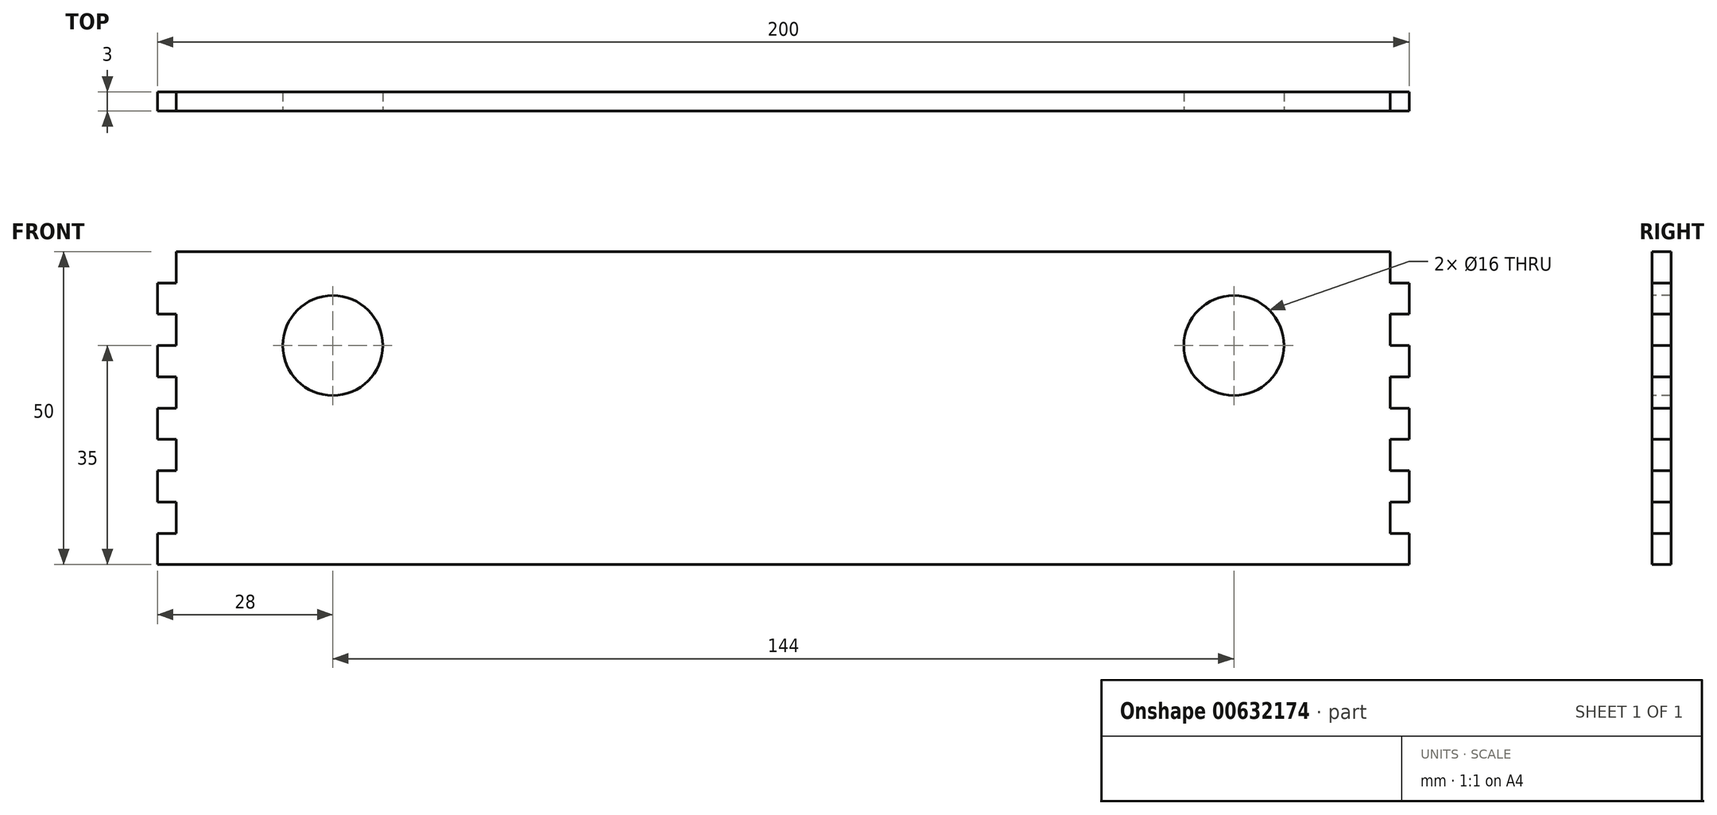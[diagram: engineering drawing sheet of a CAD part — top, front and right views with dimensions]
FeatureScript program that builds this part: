
annotation { "Feature Type Name" : "Feature", "Feature Type Description" : "" }
export const myFeature = defineFeature(function(context is Context, id is Id, definition is map)
    precondition{}
    {
        {
            var Q0;
            Q0=qCreatedBy(makeId("Front.planeOp"),FACE);
            var sketch = newSketch(context, id + "F0", { "sketchPlane" : qUnion([Q0])});
            skLineSegment(sketch, "E0.bottom", {"start": v(97, 25) * mm, "end": v(-97, 25) * mm});
            skLineSegment(sketch, "E0.top", {"start": v(97, -25) * mm, "end": v(-97, -25) * mm});
            skLineSegment(sketch, "E0.left", {"start": v(97, 25) * mm, "end": v(97, -25) * mm});
            skLineSegment(sketch, "E0.right", {"start": v(-97, 25) * mm, "end": v(-97, -25) * mm});
            skPoint(sketch, "E0.middle", {"position": v(0, 0) * mm});
            skSolve(sketch);
        }
        {
            var Q0;
            Q0=makeQuery(id+"F0.imprint","IMPRINT",FACE,{"disambiguationData":[TD([[makeQuery(id+"F0.imprint","IMPRINT",EDGE,{"derivedFrom":sQuery(id+"F0.wireOp",EDGE,"E0.bottom")}),1.0]])]});
            extrude(context, id + "F1", {"entities" : qUnion([Q0]), "depth" : 3 * mm, "offsetDistance" : 25 * mm});
        }
        {
            var Q0;
            Q0=makeQuery(id+"F1.opExtrude","CAP_FACE",FACE,{"disambiguationData":[OSD([sQuery(id+"F0.wireOp",EDGE,"E0.bottom"),sQuery(id+"F0.wireOp",EDGE,"E0.top"),sQuery(id+"F0.wireOp",EDGE,"E0.left"),sQuery(id+"F0.wireOp",EDGE,"E0.right")])],"isStart":false});
            var sketch = newSketch(context, id + "F2", { "sketchPlane" : qUnion([Q0])});
            skLineSegment(sketch, "E1.bottom", {"start": v(-97, 20) * mm, "end": v(-100, 20) * mm});
            skLineSegment(sketch, "E1.top", {"start": v(-97, 15) * mm, "end": v(-100, 15) * mm});
            skLineSegment(sketch, "E1.left", {"start": v(-97, 20) * mm, "end": v(-97, 15) * mm});
            skLineSegment(sketch, "E1.right", {"start": v(-100, 20) * mm, "end": v(-100, 15) * mm});
            skLineSegment(sketch, "E2.0.1.0", {"start": v(-97, 10) * mm, "end": v(-100, 10) * mm});
            skLineSegment(sketch, "E2.0.1.1", {"start": v(-97, 5) * mm, "end": v(-100, 5) * mm});
            skLineSegment(sketch, "E2.0.1.2", {"start": v(-97, 10) * mm, "end": v(-97, 5) * mm});
            skLineSegment(sketch, "E2.0.1.3", {"start": v(-100, 10) * mm, "end": v(-100, 5) * mm});
            skLineSegment(sketch, "E2.0.2.0", {"start": v(-97, 0) * mm, "end": v(-100, 0) * mm});
            skLineSegment(sketch, "E2.0.2.1", {"start": v(-97, -5) * mm, "end": v(-100, -5) * mm});
            skLineSegment(sketch, "E2.0.2.2", {"start": v(-97, 0) * mm, "end": v(-97, -5) * mm});
            skLineSegment(sketch, "E2.0.2.3", {"start": v(-100, 0) * mm, "end": v(-100, -5) * mm});
            skLineSegment(sketch, "E2.0.3.0", {"start": v(-97, -10) * mm, "end": v(-100, -10) * mm});
            skLineSegment(sketch, "E2.0.3.1", {"start": v(-97, -15) * mm, "end": v(-100, -15) * mm});
            skLineSegment(sketch, "E2.0.3.2", {"start": v(-97, -10) * mm, "end": v(-97, -15) * mm});
            skLineSegment(sketch, "E2.0.3.3", {"start": v(-100, -10) * mm, "end": v(-100, -15) * mm});
            skLineSegment(sketch, "E2.0.4.0", {"start": v(-97, -20) * mm, "end": v(-100, -20) * mm});
            skLineSegment(sketch, "E2.0.4.1", {"start": v(-97, -25) * mm, "end": v(-100, -25) * mm});
            skLineSegment(sketch, "E2.0.4.2", {"start": v(-97, -20) * mm, "end": v(-97, -25) * mm});
            skLineSegment(sketch, "E2.0.4.3", {"start": v(-100, -20) * mm, "end": v(-100, -25) * mm});
            skLineSegment(sketch, "E2.direction1", {"start": v(-100, 15) * mm, "end": v(-71.1, 15) * mm, "construction": true});
            skLineSegment(sketch, "E2.direction2", {"start": v(-100, 15) * mm, "end": v(-100, 5) * mm, "construction": true});
            skLineSegment(sketch, "E3.MirrorCS", {"start": v(97, 5) * mm, "end": v(100, 5) * mm});
            skLineSegment(sketch, "E4.MirrorCS", {"start": v(97, 10) * mm, "end": v(100, 10) * mm});
            skLineSegment(sketch, "E5.MirrorCS", {"start": v(100, 10) * mm, "end": v(100, 5) * mm});
            skLineSegment(sketch, "E6.MirrorCS", {"start": v(97, 10) * mm, "end": v(97, 5) * mm});
            skLineSegment(sketch, "E7.MirrorCS", {"start": v(97, 15) * mm, "end": v(100, 15) * mm});
            skLineSegment(sketch, "E8.MirrorCS", {"start": v(100, 15) * mm, "end": v(100, 5) * mm, "construction": true});
            skLineSegment(sketch, "E9.MirrorCS", {"start": v(97, 0) * mm, "end": v(100, 0) * mm});
            skLineSegment(sketch, "E10.MirrorCS", {"start": v(97, -5) * mm, "end": v(100, -5) * mm});
            skLineSegment(sketch, "E11.MirrorCS", {"start": v(100, 20) * mm, "end": v(100, 15) * mm});
            skLineSegment(sketch, "E12.MirrorCS", {"start": v(97, 20) * mm, "end": v(97, 15) * mm});
            skLineSegment(sketch, "E13.MirrorCS", {"start": v(97, 20) * mm, "end": v(100, 20) * mm});
            skLineSegment(sketch, "E14.MirrorCS", {"start": v(97, -15) * mm, "end": v(100, -15) * mm});
            skLineSegment(sketch, "E15.MirrorCS", {"start": v(97, -10) * mm, "end": v(100, -10) * mm});
            skLineSegment(sketch, "E16.MirrorCS", {"start": v(97, 0) * mm, "end": v(97, -5) * mm});
            skLineSegment(sketch, "E17.MirrorCS", {"start": v(100, -10) * mm, "end": v(100, -15) * mm});
            skLineSegment(sketch, "E18.MirrorCS", {"start": v(97, -10) * mm, "end": v(97, -15) * mm});
            skLineSegment(sketch, "E19.MirrorCS", {"start": v(97, -20) * mm, "end": v(100, -20) * mm});
            skLineSegment(sketch, "E20.MirrorCS", {"start": v(100, 0) * mm, "end": v(100, -5) * mm});
            skLineSegment(sketch, "E21.MirrorCS", {"start": v(97, -25) * mm, "end": v(100, -25) * mm});
            skLineSegment(sketch, "E22.MirrorCS", {"start": v(100, -20) * mm, "end": v(100, -25) * mm});
            skLineSegment(sketch, "E23.MirrorCS", {"start": v(97, -20) * mm, "end": v(97, -25) * mm});
            skSolve(sketch);
        }
        {
            var Q0;
            Q0=qSketchRegion(id+"F2",true);
            extrude(context, id + "F3", {"entities" : qUnion([Q0]), "operationType" : NewBodyOperationType.ADD, "oppositeDirection" : true, "depth" : 3 * mm, "offsetDistance" : 25 * mm});
        }
        {
            var Q0;
            Q0=makeQuery(id+"F3.boolean.opBoolean","MERGE",FACE,{"derivedFrom":[makeQuery(id+"F1.opExtrude","CAP_FACE",FACE,{"disambiguationData":[OSD([sQuery(id+"F0.wireOp",EDGE,"E0.bottom"),sQuery(id+"F0.wireOp",EDGE,"E0.top"),sQuery(id+"F0.wireOp",EDGE,"E0.left"),sQuery(id+"F0.wireOp",EDGE,"E0.right")])],"isStart":false}),makeQuery(id+"F3.opExtrude","CAP_FACE",FACE,{"disambiguationData":[OSD([sQuery(id+"F2.wireOp",EDGE,"E1.bottom"),sQuery(id+"F2.wireOp",EDGE,"E1.top"),sQuery(id+"F2.wireOp",EDGE,"E1.left"),sQuery(id+"F2.wireOp",EDGE,"E1.right")])],"isStart":true}),makeQuery(id+"F3.opExtrude","CAP_FACE",FACE,{"disambiguationData":[OSD([sQuery(id+"F2.wireOp",EDGE,"E2.0.1.0"),sQuery(id+"F2.wireOp",EDGE,"E2.0.1.1"),sQuery(id+"F2.wireOp",EDGE,"E2.0.1.2"),sQuery(id+"F2.wireOp",EDGE,"E2.0.1.3")])],"isStart":true}),makeQuery(id+"F3.opExtrude","CAP_FACE",FACE,{"disambiguationData":[OSD([sQuery(id+"F2.wireOp",EDGE,"E2.0.2.0"),sQuery(id+"F2.wireOp",EDGE,"E2.0.2.1"),sQuery(id+"F2.wireOp",EDGE,"E2.0.2.2"),sQuery(id+"F2.wireOp",EDGE,"E2.0.2.3")])],"isStart":true}),makeQuery(id+"F3.opExtrude","CAP_FACE",FACE,{"disambiguationData":[OSD([sQuery(id+"F2.wireOp",EDGE,"E2.0.3.0"),sQuery(id+"F2.wireOp",EDGE,"E2.0.3.1"),sQuery(id+"F2.wireOp",EDGE,"E2.0.3.2"),sQuery(id+"F2.wireOp",EDGE,"E2.0.3.3")])],"isStart":true}),makeQuery(id+"F3.opExtrude","CAP_FACE",FACE,{"disambiguationData":[OSD([sQuery(id+"F2.wireOp",EDGE,"E2.0.4.0"),sQuery(id+"F2.wireOp",EDGE,"E2.0.4.1"),sQuery(id+"F2.wireOp",EDGE,"E2.0.4.2"),sQuery(id+"F2.wireOp",EDGE,"E2.0.4.3")])],"isStart":true}),makeQuery(id+"F3.opExtrude","CAP_FACE",FACE,{"disambiguationData":[OSD([sQuery(id+"F2.wireOp",EDGE,"E3.MirrorCS"),sQuery(id+"F2.wireOp",EDGE,"E4.MirrorCS"),sQuery(id+"F2.wireOp",EDGE,"E5.MirrorCS"),sQuery(id+"F2.wireOp",EDGE,"E6.MirrorCS")])],"isStart":true}),makeQuery(id+"F3.opExtrude","CAP_FACE",FACE,{"disambiguationData":[OSD([sQuery(id+"F2.wireOp",EDGE,"E7.MirrorCS"),sQuery(id+"F2.wireOp",EDGE,"E11.MirrorCS"),sQuery(id+"F2.wireOp",EDGE,"E12.MirrorCS"),sQuery(id+"F2.wireOp",EDGE,"E13.MirrorCS")])],"isStart":true}),makeQuery(id+"F3.opExtrude","CAP_FACE",FACE,{"disambiguationData":[OSD([sQuery(id+"F2.wireOp",EDGE,"E9.MirrorCS"),sQuery(id+"F2.wireOp",EDGE,"E10.MirrorCS"),sQuery(id+"F2.wireOp",EDGE,"E16.MirrorCS"),sQuery(id+"F2.wireOp",EDGE,"E20.MirrorCS")])],"isStart":true}),makeQuery(id+"F3.opExtrude","CAP_FACE",FACE,{"disambiguationData":[OSD([sQuery(id+"F2.wireOp",EDGE,"E14.MirrorCS"),sQuery(id+"F2.wireOp",EDGE,"E15.MirrorCS"),sQuery(id+"F2.wireOp",EDGE,"E17.MirrorCS"),sQuery(id+"F2.wireOp",EDGE,"E18.MirrorCS")])],"isStart":true}),makeQuery(id+"F3.opExtrude","CAP_FACE",FACE,{"disambiguationData":[OSD([sQuery(id+"F2.wireOp",EDGE,"E19.MirrorCS"),sQuery(id+"F2.wireOp",EDGE,"E21.MirrorCS"),sQuery(id+"F2.wireOp",EDGE,"E22.MirrorCS"),sQuery(id+"F2.wireOp",EDGE,"E23.MirrorCS")])],"isStart":true})]});
            var sketch = newSketch(context, id + "F4", { "sketchPlane" : qUnion([Q0])});
            skLineSegment(sketch, "E24", {"start": v(-97, 25) * mm, "end": v(-72, 25) * mm, "construction": true});
            skLineSegment(sketch, "E25", {"start": v(-72, 25) * mm, "end": v(-72, 10) * mm, "construction": true});
            skCircle(sketch, "E26", {"center": v(-72, 10) * mm, "radius": 8 * mm});
            skCircle(sketch, "E27.MirrorC", {"center": v(72, 10) * mm, "radius": 8 * mm});
            skSolve(sketch);
        }
        {
            var Q0;
            Q0 = qSketchRegion(id + "F4", true);
            extrude(context, id + "F5", {"entities" : qUnion([Q0]), "operationType" : NewBodyOperationType.REMOVE, "oppositeDirection" : true, "depth" : 25 * mm, "offsetDistance" : 25 * mm});
        }
    });
